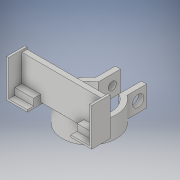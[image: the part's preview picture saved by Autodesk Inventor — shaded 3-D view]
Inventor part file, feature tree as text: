
AUTODESK INVENTOR PART (.ipt)
format: ipt  version: 2018 (Build 220112000, 112)  size: 192,512 bytes
history: native  units: in
note: dims shown in document units (in); Inventor stores cm internally (conversion verified against a paired STEP export)
features: extrude x6, sketch x6, projected_geometry x1
ambient origin geometry x8: Origin, YZ Plane, XZ Plane, XY Plane, X Axis, Y Axis, Z Axis, Center Point
bodies: Solid1 (feature_tree)
feature tree (13):
  extrude  "Extrusion1"  Depth=0.125in
  extrude  "Extrusion2"  Depth=0.125in
  extrude  "Extrusion3"  Depth=0.125in
  extrude  "Extrusion4"  Depth=0.5in
  extrude  "Extrusion5"  Depth=0.194in
  extrude  "Extrusion7"  Depth=0.17in
  sketch  "Sketch1"  dims[d0=1.05in d1=0.125in]
  sketch  "Sketch2"  dims[d2=0.125in d3=0.375in]
  sketch  "Sketch3"  dims[d4=1.0in d5=0.125in]
  sketch  "Sketch4"  dims[d6=0.5in d7=0.0in d8=0.25in]
  sketch  "Sketch5"  dims[d9=0.2in d10=0.194in]
  sketch  "Sketch7"  dims[d11=1.0in d12=0.0in d13=0.04in d14=1.0in d15=0.0in d18=0.8125in d19=0.0in d20=1.95in d21=0.975in d22=0.05in d23=0.05in d24=0.05in d25=0.05in d26=0.445in d27=0.0in d28=0.9125in d29=0.5in d30=0.05in d31=0.05in d35=0.17in d36=0.0in]
  projected_geometry  "Projected Loop3"
